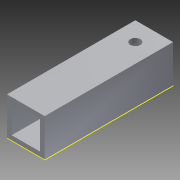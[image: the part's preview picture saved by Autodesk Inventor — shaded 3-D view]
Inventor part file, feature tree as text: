
AUTODESK INVENTOR PART (.ipt)
format: ipt  version: 2014 SP1 (Build 180222100, 222)  size: 108,032 bytes
history: native  units: in
note: dims shown in document units (in); Inventor stores cm internally (conversion verified against a paired STEP export)
features: reference x4, extrude x3, sketch x3
ambient origin geometry x8: Origin, YZ Plane, XZ Plane, XY Plane, X Axis, Y Axis, Z Axis, Center Point
bodies: Solid1 (feature_tree)
feature tree (10):
  extrude  "Extrusion1"  Depth=1.0in
  extrude  "Extrusion2"  Depth=3.4in TaperAngle=0.0deg
  extrude  "Extrusion3"  Depth=1.0in
  sketch  "Sketch1"  dims[d0=1.0in d1=1.0in]
  sketch  "Sketch2"  dims[d2=0.125in d3=3.4in d4=0.0in]
  sketch  "Sketch3"  dims[d5=0.5in d6=0.266in d7=3.4in d8=0.0in d9=1.0in d10=0.0in]
  reference  "Reference1"
  reference  "Reference2"
  reference  "Reference3"
  reference  "Reference4"
